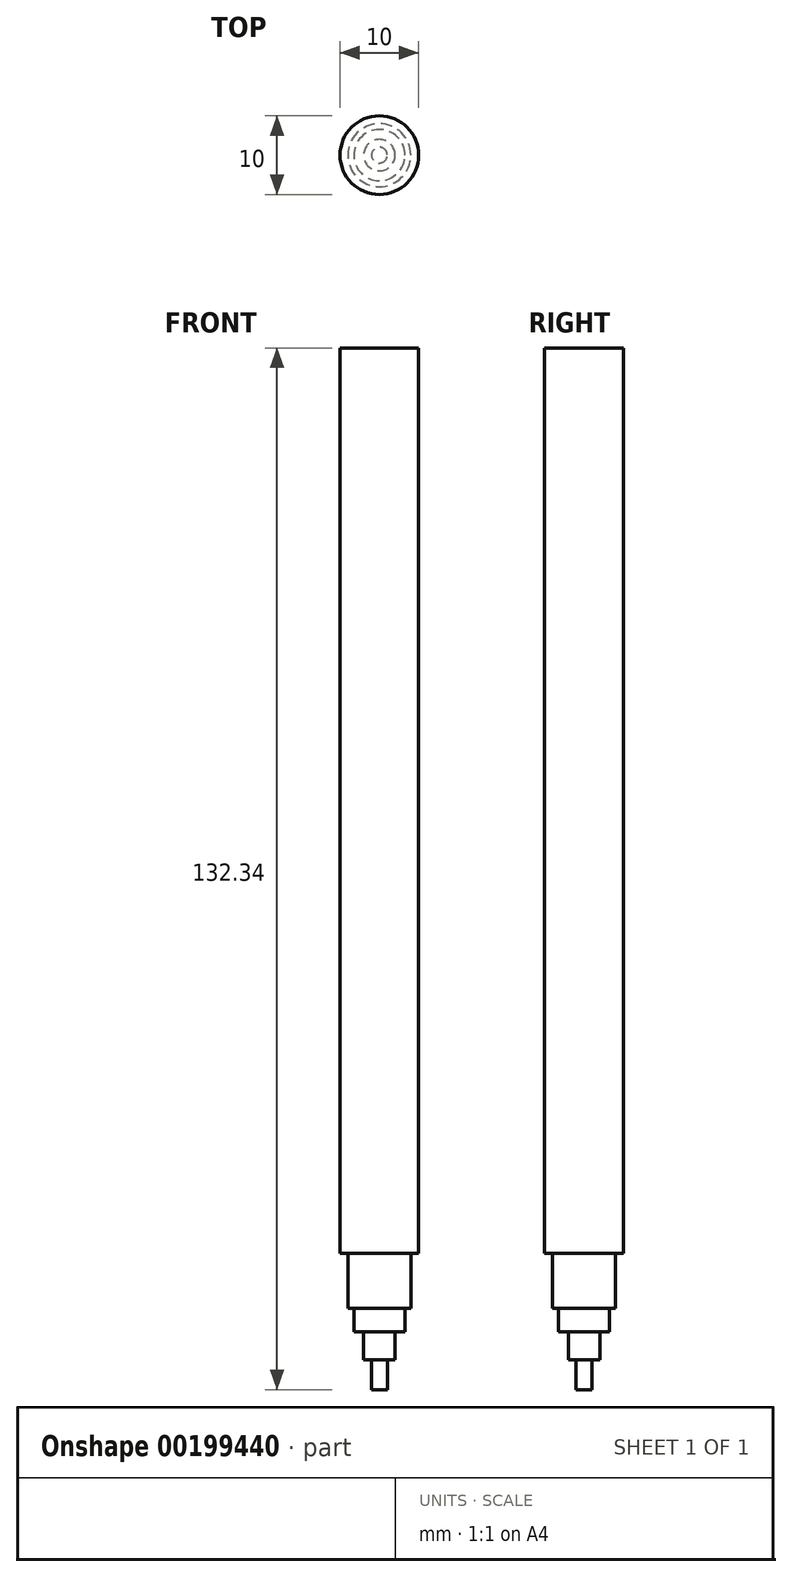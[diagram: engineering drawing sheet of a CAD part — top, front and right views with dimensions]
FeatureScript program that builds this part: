
annotation { "Feature Type Name" : "Feature", "Feature Type Description" : "" }
export const myFeature = defineFeature(function(context is Context, id is Id, definition is map)
    precondition{}
    {
        {
            var Q0;
            Q0=qCreatedBy(makeId("Top.planeOp"),FACE);
            var sketch = newSketch(context, id + "F0", { "sketchPlane" : qUnion([Q0])});
            skCircle(sketch, "E0", {"center": v(0, 0) * mm, "radius": 5 * mm});
            skSolve(sketch);
        }
        {
            var Q0;
            Q0 = qSketchRegion(id + "F0", true);
            extrude(context, id + "F1", {"entities" : qUnion([Q0]), "depth" : 70 * mm, "hasSecondDirection" : true, "secondDirectionOppositeDirection" : true, "secondDirectionDepth" : 45 * mm});
        }
        {
            var Q0;
            Q0=makeQuery(id+"F1.opExtrude","CAP_FACE",FACE,{"disambiguationData":[OSD([sQuery(id+"F0.wireOp",EDGE,"E0")])],"isStart":true});
            var sketch = newSketch(context, id + "F2", { "sketchPlane" : qUnion([Q0])});
            skCircle(sketch, "E1", {"center": v(0, 0) * mm, "radius": 4 * mm});
            skSolve(sketch);
        }
        {
            var Q0;
            Q0 = qSketchRegion(id + "F2", true);
            extrude(context, id + "F3", {"entities" : qUnion([Q0]), "operationType" : NewBodyOperationType.ADD, "depth" : 7 * mm});
        }
        {
            var Q0;
            Q0=makeQuery(id+"F3.opExtrude","CAP_FACE",FACE,{"disambiguationData":[OSD([sQuery(id+"F2.wireOp",EDGE,"E1")])],"isStart":false});
            var sketch = newSketch(context, id + "F4", { "sketchPlane" : qUnion([Q0])});
            skCircle(sketch, "E2", {"center": v(0, 0) * mm, "radius": 3.25 * mm});
            skSolve(sketch);
        }
        {
            var Q0;
            Q0 = qSketchRegion(id + "F4", true);
            extrude(context, id + "F5", {"entities" : qUnion([Q0]), "operationType" : NewBodyOperationType.ADD, "depth" : 3 * mm});
        }
        {
            var Q0;
            Q0=makeQuery(id+"F5.opExtrude","CAP_FACE",FACE,{"disambiguationData":[OSD([sQuery(id+"F4.wireOp",EDGE,"E2")])],"isStart":false});
            var sketch = newSketch(context, id + "F6", { "sketchPlane" : qUnion([Q0])});
            skCircle(sketch, "E3", {"center": v(0, 0) * mm, "radius": 2 * mm});
            skSolve(sketch);
        }
        {
            var Q0;
            Q0 = qSketchRegion(id + "F6", true);
            extrude(context, id + "F7", {"entities" : qUnion([Q0]), "operationType" : NewBodyOperationType.ADD, "depth" : 3.54 * mm});
        }
        {
            var Q0;
            Q0=makeQuery(id+"F7.opExtrude","CAP_FACE",FACE,{"disambiguationData":[OSD([sQuery(id+"F6.wireOp",EDGE,"E3")])],"isStart":false});
            var sketch = newSketch(context, id + "F8", { "sketchPlane" : qUnion([Q0])});
            skCircle(sketch, "E4", {"center": v(0, 0) * mm, "radius": 1 * mm});
            skSolve(sketch);
        }
        {
            var Q0;
            Q0 = qSketchRegion(id + "F8", true);
            extrude(context, id + "F9", {"entities" : qUnion([Q0]), "operationType" : NewBodyOperationType.ADD, "depth" : 3.8 * mm});
        }
    });
